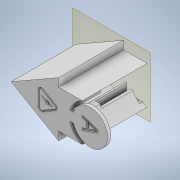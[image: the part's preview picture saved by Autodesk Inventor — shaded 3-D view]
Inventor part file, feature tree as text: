
AUTODESK INVENTOR PART (.ipt)
format: ipt  version: 2022.3 (Build 263350000, 350)  size: 297,472 bytes
history: native  units: mm
features: sketch x7, extrude x5, reference x4, projected_geometry x4, emboss x2, other x2, plane x1
ambient origin geometry x8: Origin, YZ Plane, XZ Plane, XY Plane, X Axis, Y Axis, Z Axis, Center Point
bodies: Solid1 (feature_tree)
feature tree (25):
  plane  "Work Plane1"
  extrude  "Extrusion1"  Depth=2.0mm TaperAngle=0.0deg
  extrude  "Extrusion2"  Depth=0.2mm
  extrude  "Extrusion3"  Depth=1.0mm
  extrude  "Extrusion4"  Depth=17.0mm TaperAngle=0.0deg
  extrude  "Extrusion5"  Depth=22.0mm
  sketch  "Sketch6"  dims[d20=22.0mm]
  emboss  "Emboss2"
  emboss  "Emboss3"
  sketch  "Sketch1"  dims[d0=41.0mm d1=0.0mm d2=2.0mm d3=0.0mm]
  reference  "Reference1"
  sketch  "Sketch2"  dims[d4=0.2mm d5=0.2mm]
  projected_geometry  "Projected Loop1"
  reference  "Reference2"
  sketch  "Sketch3"  dims[d6=1.0mm d7=1.0mm]
  reference  "Reference3"
  reference  "Reference4"
  projected_geometry  "Projected Loop2"
  sketch  "Sketch4"  dims[d8=37.0mm d9=0.0mm d10=17.0mm d11=0.0mm]
  projected_geometry  "Projected Loop3"
  sketch  "Sketch5"  dims[d12=17.0mm d13=0.0mm d19=22.0mm]
  projected_geometry  "Projected Loop4"
  sketch  "Sketch7"  dims[d21=22.0mm d22=22.0mm d23=0.0mm d24=0.0mm d25=1.0mm d26=0.0mm d28=1.0mm d29=1.0mm d30=0.75mm d31=1.0mm d32=0.0mm]
  other  "v2.0.iam"
  other  "Base:1"
